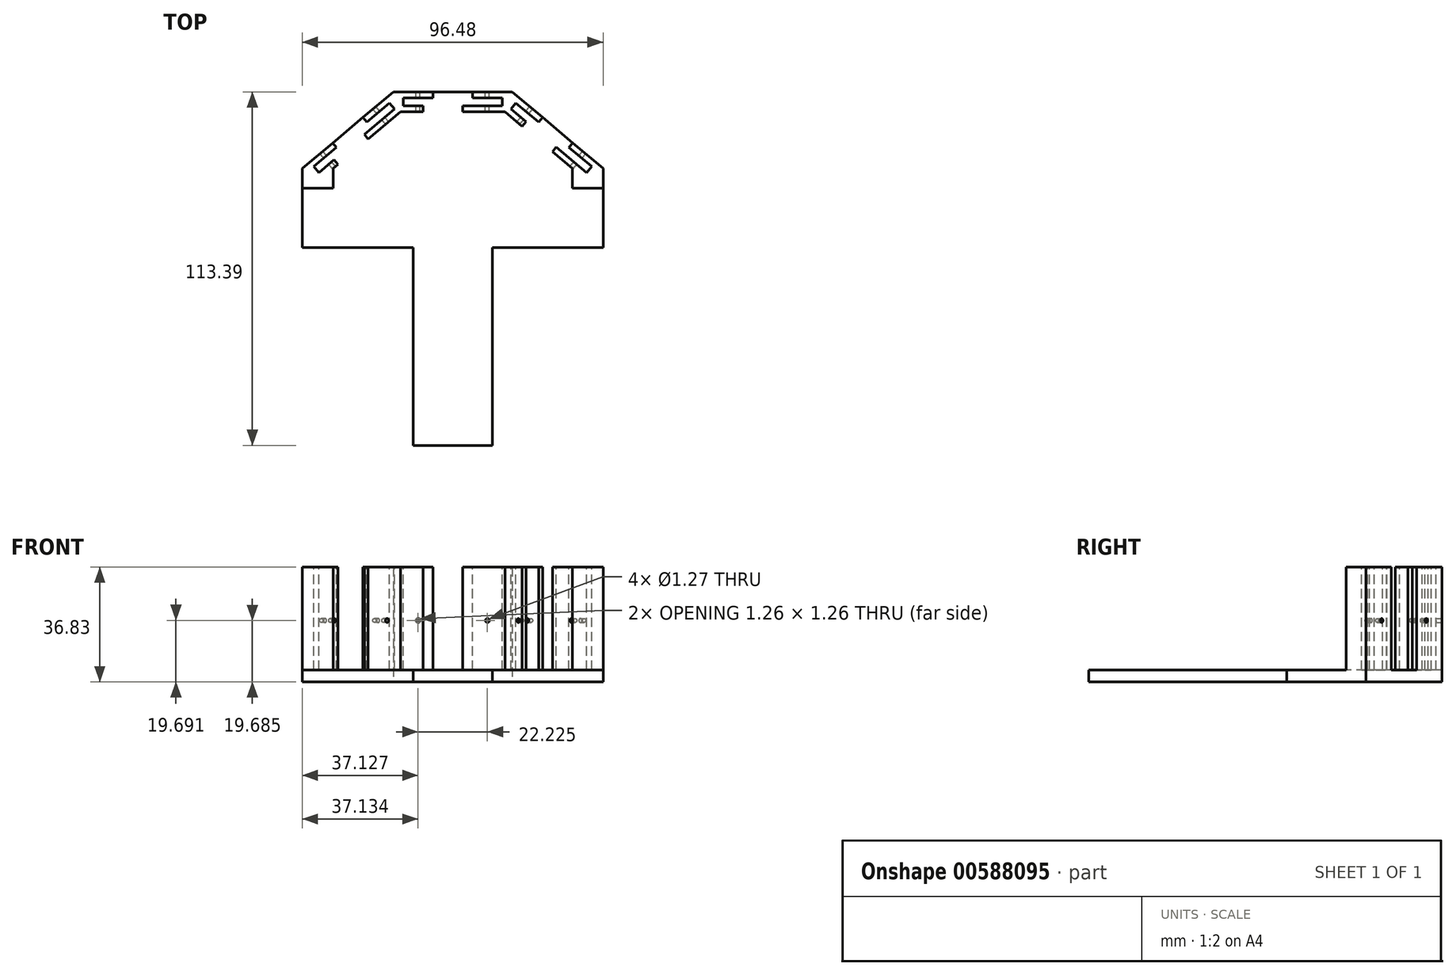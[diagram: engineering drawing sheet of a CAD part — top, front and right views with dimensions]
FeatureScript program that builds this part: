
annotation { "Feature Type Name" : "Feature", "Feature Type Description" : "" }
export const myFeature = defineFeature(function(context is Context, id is Id, definition is map)
    precondition{}
    {
        {
            var Q0;
            Q0=qCreatedBy(makeId("Top.planeOp"),FACE);
            var sketch = newSketch(context, id + "F0", { "sketchPlane" : qUnion([Q0])});
            skLineSegment(sketch, "E0", {"start": v(-48.24, 0) * mm, "end": v(-19.05, 24.5) * mm});
            skLineSegment(sketch, "E1", {"start": v(-19.05, 24.5) * mm, "end": v(19.05, 24.5) * mm});
            skLineSegment(sketch, "E2", {"start": v(19.05, 24.5) * mm, "end": v(48.24, 0) * mm});
            skLineSegment(sketch, "E3", {"start": v(48.24, 0) * mm, "end": v(48.24, -25.4) * mm});
            skLineSegment(sketch, "E4", {"start": v(48.24, -25.4) * mm, "end": v(-48.24, -25.4) * mm});
            skLineSegment(sketch, "E5", {"start": v(-48.24, -25.4) * mm, "end": v(-48.24, 0) * mm});
            skLineSegment(sketch, "E6", {"start": v(0, 0) * mm, "end": v(0, 24.5) * mm, "construction": true});
            skSolve(sketch);
        }
        {
            var Q0;
            Q0 = qSketchRegion(id + "F0", true);
            extrude(context, id + "F1", {"entities" : qUnion([Q0]), "depth" : 36.83 * mm, "offsetDistance" : 25.4 * mm});
        }
        {
            var Q0;
            Q0=makeQuery(id+"F1.opExtrude","CAP_FACE",FACE,{"disambiguationData":[OSD([sQuery(id+"F0.wireOp",EDGE,"E0"),sQuery(id+"F0.wireOp",EDGE,"E1"),sQuery(id+"F0.wireOp",EDGE,"E2"),sQuery(id+"F0.wireOp",EDGE,"E3"),sQuery(id+"F0.wireOp",EDGE,"E4"),sQuery(id+"F0.wireOp",EDGE,"E5")])],"isStart":false});
            var sketch = newSketch(context, id + "F2", { "sketchPlane" : qUnion([Q0])});
            skLineSegment(sketch, "E7", {"start": v(-38.36, -25.4) * mm, "end": v(-38.36, 0) * mm, "construction": true});
            skLineSegment(sketch, "E8", {"start": v(-38.36, 0) * mm, "end": v(-16.74, 18.14) * mm});
            skLineSegment(sketch, "E9", {"start": v(-16.74, 18.14) * mm, "end": v(16.74, 18.14) * mm});
            skLineSegment(sketch, "E10", {"start": v(16.74, 18.14) * mm, "end": v(38.36, 0) * mm});
            skLineSegment(sketch, "E11", {"start": v(38.36, 0) * mm, "end": v(38.36, -25.4) * mm, "construction": true});
            skLineSegment(sketch, "E12", {"start": v(38.36, -25.4) * mm, "end": v(-38.36, -25.4) * mm});
            skLineSegment(sketch, "E13", {"start": v(0, 0) * mm, "end": v(0, 24.5) * mm, "construction": true});
            skLineSegment(sketch, "E14", {"start": v(-38.36, 0) * mm, "end": v(-38.36, -6.35) * mm});
            skLineSegment(sketch, "E15", {"start": v(-38.36, -6.35) * mm, "end": v(-48.24, -6.35) * mm});
            skLineSegment(sketch, "E16", {"start": v(-48.24, -6.35) * mm, "end": v(-48.24, -25.4) * mm});
            skLineSegment(sketch, "E17", {"start": v(-48.24, -25.4) * mm, "end": v(48.24, -25.4) * mm});
            skLineSegment(sketch, "E18", {"start": v(48.24, -25.4) * mm, "end": v(48.24, -6.35) * mm});
            skLineSegment(sketch, "E19", {"start": v(48.24, -6.35) * mm, "end": v(38.36, -6.35) * mm});
            skLineSegment(sketch, "E20", {"start": v(38.36, -6.35) * mm, "end": v(38.36, 0) * mm});
            skSolve(sketch);
        }
        {
            var Q0;
            Q0 = qSketchRegion(id + "F2", true);
            extrude(context, id + "F3", {"entities" : qUnion([Q0]), "operationType" : NewBodyOperationType.REMOVE, "oppositeDirection" : true, "depth" : 33.02 * mm, "offsetDistance" : 25.4 * mm});
        }
        {
            var Q0;
            Q0=makeQuery(id+"F1.opExtrude","CAP_FACE",FACE,{"disambiguationData":[OSD([sQuery(id+"F0.wireOp",EDGE,"E0"),sQuery(id+"F0.wireOp",EDGE,"E1"),sQuery(id+"F0.wireOp",EDGE,"E2"),sQuery(id+"F0.wireOp",EDGE,"E3"),sQuery(id+"F0.wireOp",EDGE,"E4"),sQuery(id+"F0.wireOp",EDGE,"E5")])],"isStart":false});
            var sketch = newSketch(context, id + "F4", { "sketchPlane" : qUnion([Q0])});
            skLineSegment(sketch, "E21", {"start": v(0, 18.14) * mm, "end": v(0, 21.32) * mm, "construction": true});
            skLineSegment(sketch, "E22.1.0", {"start": v(-15.87, 21.32) * mm, "end": v(15.88, 21.32) * mm, "construction": true});
            skLineSegment(sketch, "E22.1.1", {"start": v(6.35, 22.59) * mm, "end": v(15.88, 22.59) * mm});
            skLineSegment(sketch, "E22.1.2", {"start": v(15.88, 20.05) * mm, "end": v(3.18, 20.05) * mm});
            skLineSegment(sketch, "E22.1.3", {"start": v(3.17, 18.14) * mm, "end": v(-9.52, 18.14) * mm});
            skLineSegment(sketch, "E22.1.4", {"start": v(-15.88, 22.59) * mm, "end": v(-6.35, 22.59) * mm});
            skLineSegment(sketch, "E22.1.5", {"start": v(-6.35, 24.5) * mm, "end": v(6.35, 24.5) * mm});
            skLineSegment(sketch, "E22.1.6", {"start": v(0, 21.32) * mm, "end": v(0, 24.5) * mm, "construction": true});
            skLineSegment(sketch, "E22.1.8", {"start": v(-9.52, 20.05) * mm, "end": v(-15.88, 20.05) * mm});
            skLineSegment(sketch, "E22.1.9", {"start": v(-15.88, 20.05) * mm, "end": v(-15.88, 22.59) * mm});
            skLineSegment(sketch, "E22.1.10", {"start": v(-9.52, 18.14) * mm, "end": v(-9.52, 20.05) * mm});
            skLineSegment(sketch, "E22.1.11", {"start": v(6.35, 24.5) * mm, "end": v(6.35, 22.59) * mm});
            skLineSegment(sketch, "E22.1.12", {"start": v(3.18, 20.05) * mm, "end": v(3.18, 18.14) * mm});
            skLineSegment(sketch, "E22.1.13", {"start": v(-6.35, 22.59) * mm, "end": v(-6.35, 24.5) * mm});
            skLineSegment(sketch, "E22.1.14", {"start": v(15.88, 22.59) * mm, "end": v(15.88, 20.05) * mm});
            skPoint(sketch, "E22.center", {"position": v(0, 0) * mm});
            skPoint(sketch, "E23.1.5", {"position": v(15.88, 20.05) * mm});
            skPoint(sketch, "E24", {"position": v(0, 24.5) * mm});
            skLineSegment(sketch, "E25.1.0", {"start": v(32, 5.34) * mm, "end": v(22.26, 13.5) * mm});
            skPoint(sketch, "E25.1.1", {"position": v(42.95, -1.36) * mm});
            skLineSegment(sketch, "E25.1.2", {"start": v(28.78, 16.33) * mm, "end": v(38.5, 8.16) * mm});
            skLineSegment(sketch, "E25.1.3", {"start": v(20.26, 21) * mm, "end": v(27.55, 14.87) * mm});
            skLineSegment(sketch, "E25.1.4", {"start": v(37.28, 6.7) * mm, "end": v(44.58, 0.58) * mm});
            skLineSegment(sketch, "E25.1.5", {"start": v(42.95, -1.36) * mm, "end": v(33.22, 6.8) * mm});
            skPoint(sketch, "E25.1.6", {"position": v(33.64, 12.25) * mm});
            skLineSegment(sketch, "E25.1.7", {"start": v(19.44, 20.02) * mm, "end": v(43.76, -0.4) * mm, "construction": true});
            skLineSegment(sketch, "E25.1.8", {"start": v(29.56, 7.38) * mm, "end": v(31.6, 9.81) * mm, "construction": true});
            skLineSegment(sketch, "E25.1.9", {"start": v(31.6, 9.81) * mm, "end": v(33.64, 12.25) * mm, "construction": true});
            skLineSegment(sketch, "E25.1.10", {"start": v(23.49, 14.96) * mm, "end": v(18.63, 19.04) * mm});
            skLineSegment(sketch, "E25.1.11", {"start": v(27.55, 14.87) * mm, "end": v(28.78, 16.33) * mm});
            skLineSegment(sketch, "E25.1.12", {"start": v(44.58, 0.58) * mm, "end": v(42.95, -1.36) * mm});
            skLineSegment(sketch, "E25.1.13", {"start": v(18.63, 19.04) * mm, "end": v(20.26, 21) * mm});
            skLineSegment(sketch, "E25.1.14", {"start": v(38.5, 8.16) * mm, "end": v(37.28, 6.7) * mm});
            skLineSegment(sketch, "E25.1.15", {"start": v(33.22, 6.8) * mm, "end": v(32, 5.34) * mm});
            skLineSegment(sketch, "E25.1.16", {"start": v(22.26, 13.5) * mm, "end": v(23.49, 14.96) * mm});
            skPoint(sketch, "E25.center", {"position": v(0, -27.85) * mm});
            skLineSegment(sketch, "E25.anchor1", {"start": v(0, -27.85) * mm, "end": v(-15.87, 20.05) * mm, "construction": true});
            skLineSegment(sketch, "E25.anchor2", {"start": v(0, -27.85) * mm, "end": v(18.63, 19.04) * mm, "construction": true});
            skLineSegment(sketch, "E26.1.0", {"start": v(-38.08, 2.72) * mm, "end": v(-42.95, -1.36) * mm});
            skLineSegment(sketch, "E26.1.1", {"start": v(-31.6, 9.81) * mm, "end": v(-33.64, 12.25) * mm, "construction": true});
            skPoint(sketch, "E26.1.2", {"position": v(-18.63, 19.04) * mm});
            skLineSegment(sketch, "E26.1.3", {"start": v(-18.63, 19.04) * mm, "end": v(-28.35, 10.88) * mm});
            skLineSegment(sketch, "E26.1.4", {"start": v(-27.55, 14.87) * mm, "end": v(-20.26, 21) * mm});
            skLineSegment(sketch, "E26.1.5", {"start": v(-38.5, 8.16) * mm, "end": v(-28.78, 16.33) * mm});
            skLineSegment(sketch, "E26.1.6", {"start": v(-29.56, 7.38) * mm, "end": v(-31.6, 9.81) * mm, "construction": true});
            skLineSegment(sketch, "E26.1.7", {"start": v(-44.58, 0.58) * mm, "end": v(-37.28, 6.7) * mm});
            skPoint(sketch, "E26.1.8", {"position": v(-33.64, 12.25) * mm});
            skLineSegment(sketch, "E26.1.9", {"start": v(-27.13, 9.42) * mm, "end": v(-36.86, 1.26) * mm});
            skLineSegment(sketch, "E26.1.10", {"start": v(-43.76, -0.4) * mm, "end": v(-19.44, 20.02) * mm, "construction": true});
            skLineSegment(sketch, "E26.1.11", {"start": v(-20.26, 21) * mm, "end": v(-18.63, 19.04) * mm});
            skLineSegment(sketch, "E26.1.12", {"start": v(-42.95, -1.36) * mm, "end": v(-44.58, 0.58) * mm});
            skLineSegment(sketch, "E26.1.13", {"start": v(-37.28, 6.7) * mm, "end": v(-38.5, 8.16) * mm});
            skLineSegment(sketch, "E26.1.14", {"start": v(-28.78, 16.33) * mm, "end": v(-27.55, 14.87) * mm});
            skLineSegment(sketch, "E26.1.15", {"start": v(-28.35, 10.88) * mm, "end": v(-27.13, 9.42) * mm});
            skLineSegment(sketch, "E26.1.16", {"start": v(-36.86, 1.26) * mm, "end": v(-38.08, 2.72) * mm});
            skLineSegment(sketch, "E26.anchor1", {"start": v(0, -27.85) * mm, "end": v(32, 5.34) * mm, "construction": true});
            skLineSegment(sketch, "E26.anchor2", {"start": v(0, -27.85) * mm, "end": v(-27.13, 9.42) * mm, "construction": true});
            skSolve(sketch);
        }
        {
            var Q0;
            Q0 = qSketchRegion(id + "F4", true);
            extrude(context, id + "F5", {"entities" : qUnion([Q0]), "operationType" : NewBodyOperationType.REMOVE, "oppositeDirection" : true, "depth" : 33.02 * mm, "offsetDistance" : 25.4 * mm});
        }
        {
            var Q0;
            Q0=makeQuery(id+"F1.opExtrude","SWEPT_FACE",FACE,{"disambiguationData":[OSD([sQuery(id+"F0.wireOp",EDGE,"E0")])]});
            var sketch = newSketch(context, id + "F6", { "sketchPlane" : qUnion([Q0])});
            skLineSegment(sketch, "E27", {"start": v(-1.15, 19.68) * mm, "end": v(36.95, 19.68) * mm, "construction": true});
            skCircle(sketch, "E28", {"center": v(6.79, 19.68) * mm, "radius": 0.64 * mm});
            skCircle(sketch, "E29", {"center": v(29.01, 19.68) * mm, "radius": 0.64 * mm});
            skLineSegment(sketch, "E30", {"start": v(6.79, 19.68) * mm, "end": v(17.9, 0) * mm, "construction": true});
            skLineSegment(sketch, "E31", {"start": v(29.01, 19.68) * mm, "end": v(17.9, 0) * mm, "construction": true});
            skSolve(sketch);
        }
        {
            var Q0;
            Q0 = qSketchRegion(id + "F6", true);
            var Q1;
            {var subQ1=sQuery(id+"F2.wireOp",EDGE,"E9");var subQ2=sQuery(id+"F2.wireOp",EDGE,"E8");Q1=makeQuery(id+"F5.boolean.opBoolean","SPLIT",FACE,{"disambiguationData":[TD([makeQuery(id+"F3.boolean.opBoolean","COPY",FACE,{"derivedFrom":makeQuery(id+"F3.opExtrude","SWEPT_FACE",FACE,{"disambiguationData":[OSD([subQ1])]})})])],"derivedFrom":makeQuery(id+"F3.boolean.opBoolean","COPY",FACE,{"derivedFrom":makeQuery(id+"F3.opExtrude","SWEPT_FACE",FACE,{"disambiguationData":[OSD([subQ2])]})})});}
            extrude(context, id + "F7", {"entities" : qUnion([Q0]), "operationType" : NewBodyOperationType.REMOVE, "endBound" : BoundingType.UP_TO_SURFACE, "oppositeDirection" : true, "depth" : 25.4 * mm, "endBoundEntityFace" : qUnion([Q1]), "offsetDistance" : 25.4 * mm});
        }
        {
            var Q0;
            Q0=makeQuery(id+"F1.opExtrude","SWEPT_FACE",FACE,{"disambiguationData":[OSD([sQuery(id+"F0.wireOp",EDGE,"E1")])]});
            var sketch = newSketch(context, id + "F8", { "sketchPlane" : qUnion([Q0])});
            skLineSegment(sketch, "E32", {"start": v(0, 0) * mm, "end": v(-11.11, 19.68) * mm, "construction": true});
            skLineSegment(sketch, "E33", {"start": v(-19.05, 19.68) * mm, "end": v(19.05, 19.68) * mm, "construction": true});
            skLineSegment(sketch, "E34", {"start": v(0, 0) * mm, "end": v(11.11, 19.68) * mm, "construction": true});
            skCircle(sketch, "E35", {"center": v(-11.11, 19.68) * mm, "radius": 0.64 * mm});
            skCircle(sketch, "E36", {"center": v(11.11, 19.68) * mm, "radius": 0.64 * mm});
            skSolve(sketch);
        }
        {
            var Q0;
            Q0=makeQuery(id+"F1.opExtrude","SWEPT_FACE",FACE,{"disambiguationData":[OSD([sQuery(id+"F0.wireOp",EDGE,"E2")])]});
            var sketch = newSketch(context, id + "F9", { "sketchPlane" : qUnion([Q0])});
            skLineSegment(sketch, "E37", {"start": v(-36.95, 19.68) * mm, "end": v(1.15, 19.68) * mm, "construction": true});
            skLineSegment(sketch, "E38", {"start": v(-29.01, 19.68) * mm, "end": v(-17.9, 0) * mm, "construction": true});
            skLineSegment(sketch, "E39", {"start": v(-17.9, 0) * mm, "end": v(-6.79, 19.68) * mm, "construction": true});
            skCircle(sketch, "E40", {"center": v(-29.01, 19.68) * mm, "radius": 0.64 * mm});
            skCircle(sketch, "E41", {"center": v(-6.79, 19.68) * mm, "radius": 0.64 * mm});
            skSolve(sketch);
        }
        {
            var Q0;
            Q0 = qSketchRegion(id + "F9", true);
            var Q1;
            {var subQ0=sQuery(id+"F2.wireOp",EDGE,"E20");var subQ1=sQuery(id+"F2.wireOp",EDGE,"E10");Q1=makeQuery(id+"F5.boolean.opBoolean","SPLIT",FACE,{"disambiguationData":[TD([makeQuery(id+"F3.boolean.opBoolean","COPY",FACE,{"derivedFrom":makeQuery(id+"F3.opExtrude","SWEPT_FACE",FACE,{"disambiguationData":[OSD([subQ0])]})})])],"derivedFrom":makeQuery(id+"F3.boolean.opBoolean","COPY",FACE,{"derivedFrom":makeQuery(id+"F3.opExtrude","SWEPT_FACE",FACE,{"disambiguationData":[OSD([subQ1])]})})});}
            extrude(context, id + "F10", {"entities" : qUnion([Q0]), "operationType" : NewBodyOperationType.REMOVE, "endBound" : BoundingType.UP_TO_SURFACE, "oppositeDirection" : true, "depth" : 25.4 * mm, "endBoundEntityFace" : qUnion([Q1]), "offsetDistance" : 25.4 * mm});
        }
        {
            var Q0;
            Q0 = qSketchRegion(id + "F8", true);
            var Q1;
            {var subQ0=sQuery(id+"F2.wireOp",EDGE,"E10");var subQ2=sQuery(id+"F2.wireOp",EDGE,"E9");Q1=makeQuery(id+"F5.boolean.opBoolean","SPLIT",FACE,{"disambiguationData":[TD([makeQuery(id+"F3.boolean.opBoolean","COPY",FACE,{"derivedFrom":makeQuery(id+"F3.opExtrude","SWEPT_FACE",FACE,{"disambiguationData":[OSD([subQ0])]})})])],"derivedFrom":makeQuery(id+"F3.boolean.opBoolean","COPY",FACE,{"derivedFrom":makeQuery(id+"F3.opExtrude","SWEPT_FACE",FACE,{"disambiguationData":[OSD([subQ2])]})})});}
            extrude(context, id + "F11", {"entities" : qUnion([Q0]), "operationType" : NewBodyOperationType.REMOVE, "endBound" : BoundingType.UP_TO_SURFACE, "oppositeDirection" : true, "depth" : 25.4 * mm, "endBoundEntityFace" : qUnion([Q1]), "offsetDistance" : 25.4 * mm});
        }
        {
            var Q0;
            Q0=makeQuery(id+"F1.opExtrude","CAP_FACE",FACE,{"disambiguationData":[OSD([sQuery(id+"F0.wireOp",EDGE,"E0"),sQuery(id+"F0.wireOp",EDGE,"E1"),sQuery(id+"F0.wireOp",EDGE,"E2"),sQuery(id+"F0.wireOp",EDGE,"E3"),sQuery(id+"F0.wireOp",EDGE,"E4"),sQuery(id+"F0.wireOp",EDGE,"E5")])],"isStart":true});
            var sketch = newSketch(context, id + "F12", { "sketchPlane" : qUnion([Q0])});
            skLineSegment(sketch, "E42.bottom", {"start": v(-12.7, 25.4) * mm, "end": v(12.7, 25.4) * mm});
            skLineSegment(sketch, "E42.top", {"start": v(-12.7, 88.9) * mm, "end": v(12.7, 88.9) * mm});
            skLineSegment(sketch, "E42.left", {"start": v(-12.7, 25.4) * mm, "end": v(-12.7, 88.9) * mm});
            skLineSegment(sketch, "E42.right", {"start": v(12.7, 25.4) * mm, "end": v(12.7, 88.9) * mm});
            skLineSegment(sketch, "E43", {"start": v(0, 0) * mm, "end": v(0, 88.9) * mm, "construction": true});
            skSolve(sketch);
        }
        {
            var Q0;
            Q0 = qSketchRegion(id + "F12", true);
            var Q1;
            Q1=makeQuery(id+"F5.boolean.opBoolean","MERGE",FACE,{"derivedFrom":[makeQuery(id+"F3.boolean.opBoolean","COPY",FACE,{"derivedFrom":makeQuery(id+"F3.opExtrude","CAP_FACE",FACE,{"disambiguationData":[OSD([sQuery(id+"F2.wireOp",EDGE,"E8"),sQuery(id+"F2.wireOp",EDGE,"E9"),sQuery(id+"F2.wireOp",EDGE,"E10"),sQuery(id+"F2.wireOp",EDGE,"E14"),sQuery(id+"F2.wireOp",EDGE,"E15"),sQuery(id+"F2.wireOp",EDGE,"E16"),sQuery(id+"F2.wireOp",EDGE,"E17"),sQuery(id+"F2.wireOp",EDGE,"E18"),sQuery(id+"F2.wireOp",EDGE,"E19"),sQuery(id+"F2.wireOp",EDGE,"E20")])],"isStart":false})}),makeQuery(id+"F5.opExtrude","CAP_FACE",FACE,{"disambiguationData":[OSD([sQuery(id+"F4.wireOp",EDGE,"7iILYdmB-3I0J-8KAK-w3p4-ulub1nFzPw0I"),sQuery(id+"F4.wireOp",EDGE,"tjLjwkNP-0101-HItq-5a0M-vE2Nvji9DEPE"),sQuery(id+"F4.wireOp",EDGE,"OIeooSSA-ci0i-ATzq-gk7c-2Fi9NC00eRca"),sQuery(id+"F4.wireOp",EDGE,"mzoOGwUS-6JON-fSrQ-RUM1-MoMvOygfF9TD"),sQuery(id+"F4.wireOp",EDGE,"vV20OTmg-pYBK-jRdC-RUSO-FnU1It1wM9iA"),sQuery(id+"F4.wireOp",EDGE,"c2B8ZrnY-pkTp-hZnU-cKjW-oe4HCCWWtqAL"),sQuery(id+"F4.wireOp",EDGE,"F5d6c3Oc-LngO-0mYg-hxNS-oSwu72vhgzzZ"),sQuery(id+"F4.wireOp",EDGE,"t2MvxifX-MUMb-G0fD-tpDl-dhOVdtUguWCs"),sQuery(id+"F4.wireOp",EDGE,"n0D8afo8-rT6i-5yWE-VYlP-BU2fep9iAtQ6"),sQuery(id+"F4.wireOp",EDGE,"lf6t2Ise-nBVB-dv9s-gFHG-lyg8V8V4SOtn"),sQuery(id+"F4.wireOp",EDGE,"QoMSu0Kl-iWv6-fQGy-0PWv-3nTKNURXWiVB"),sQuery(id+"F4.wireOp",EDGE,"Ex11wZCD-ldO3-FSSC-8r7Q-qjJmWizB1IFI")])],"isStart":false}),makeQuery(id+"F5.opExtrude","CAP_FACE",FACE,{"disambiguationData":[OSD([sQuery(id+"F4.wireOp",EDGE,"E22.1.1"),sQuery(id+"F4.wireOp",EDGE,"E22.1.2"),sQuery(id+"F4.wireOp",EDGE,"E22.1.3"),sQuery(id+"F4.wireOp",EDGE,"E22.1.4"),sQuery(id+"F4.wireOp",EDGE,"E22.1.5"),sQuery(id+"F4.wireOp",EDGE,"E22.1.8"),sQuery(id+"F4.wireOp",EDGE,"E22.1.9"),sQuery(id+"F4.wireOp",EDGE,"E22.1.10"),sQuery(id+"F4.wireOp",EDGE,"E22.1.11"),sQuery(id+"F4.wireOp",EDGE,"E22.1.12"),sQuery(id+"F4.wireOp",EDGE,"E22.1.13"),sQuery(id+"F4.wireOp",EDGE,"E22.1.14")])],"isStart":false}),makeQuery(id+"F5.opExtrude","CAP_FACE",FACE,{"disambiguationData":[OSD([sQuery(id+"F4.wireOp",EDGE,"E23.1.0"),sQuery(id+"F4.wireOp",EDGE,"E23.1.4"),sQuery(id+"F4.wireOp",EDGE,"E23.1.6"),sQuery(id+"F4.wireOp",EDGE,"E23.1.7"),sQuery(id+"F4.wireOp",EDGE,"E23.1.8"),sQuery(id+"F4.wireOp",EDGE,"E23.1.9"),sQuery(id+"F4.wireOp",EDGE,"E23.1.11"),sQuery(id+"F4.wireOp",EDGE,"E23.1.12"),sQuery(id+"F4.wireOp",EDGE,"E23.1.13"),sQuery(id+"F4.wireOp",EDGE,"E23.1.14"),sQuery(id+"F4.wireOp",EDGE,"E23.1.15"),sQuery(id+"F4.wireOp",EDGE,"E23.1.16")])],"isStart":false})]});
            extrude(context, id + "F13", {"entities" : qUnion([Q0]), "operationType" : NewBodyOperationType.ADD, "endBound" : BoundingType.UP_TO_SURFACE, "oppositeDirection" : true, "depth" : 25.4 * mm, "endBoundEntityFace" : qUnion([Q1]), "offsetDistance" : 25.4 * mm});
        }
    });
